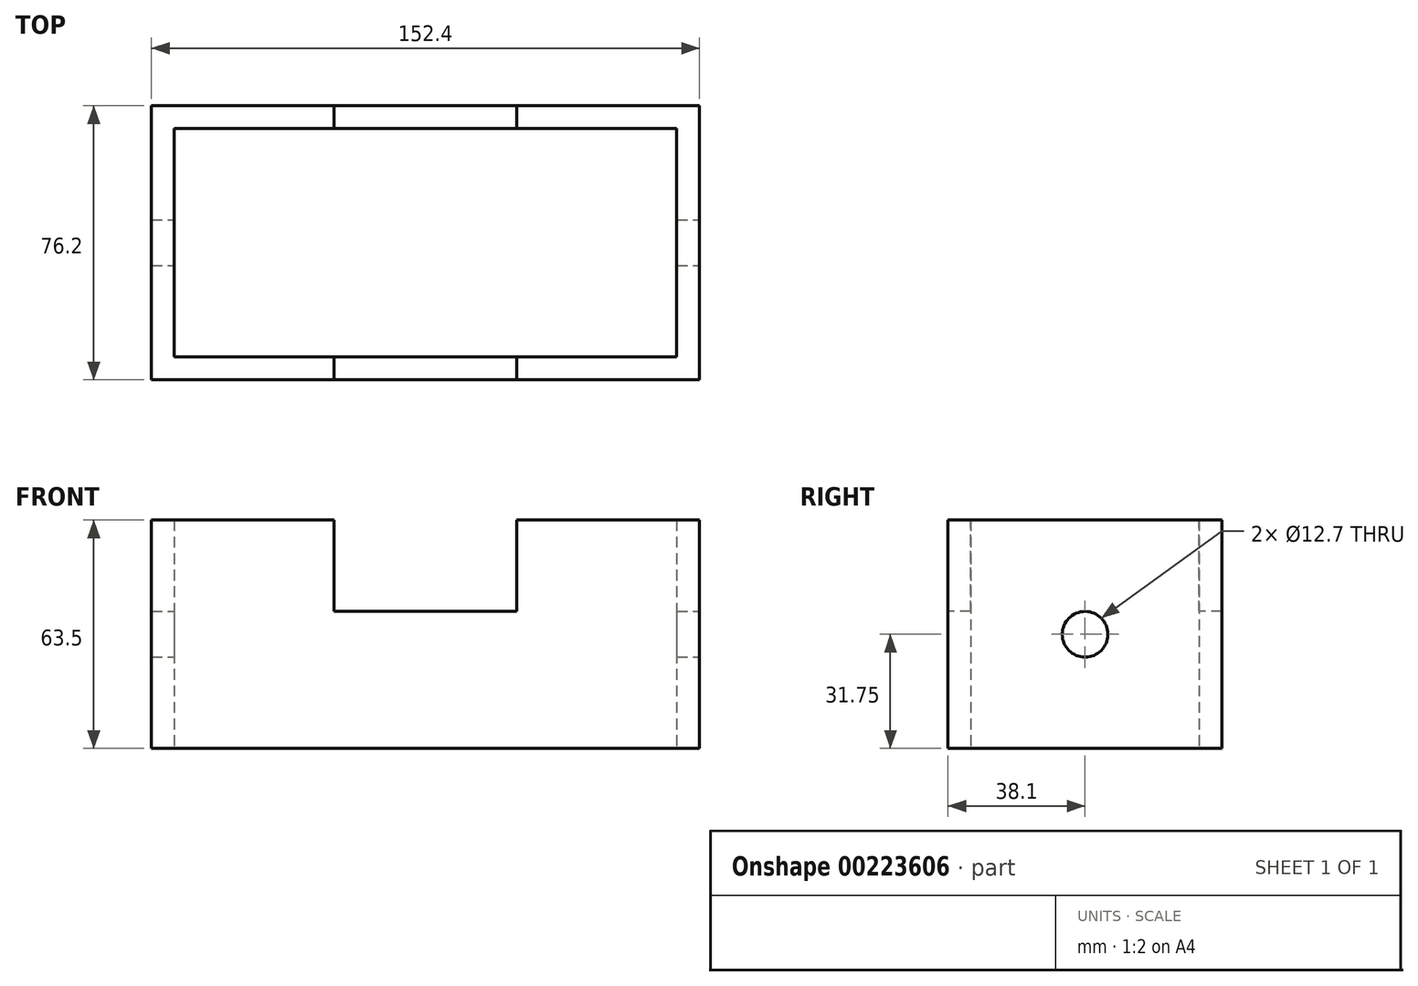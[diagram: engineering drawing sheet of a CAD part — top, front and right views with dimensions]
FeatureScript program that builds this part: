
annotation { "Feature Type Name" : "Feature", "Feature Type Description" : "" }
export const myFeature = defineFeature(function(context is Context, id is Id, definition is map)
    precondition{}
    {
        {
            var Q0;
            Q0=qCreatedBy(makeId("Top.planeOp"),FACE);
            var sketch = newSketch(context, id + "F0", { "sketchPlane" : qUnion([Q0])});
            skLineSegment(sketch, "E0.bottom", {"start": v(-76.2, -38.1) * mm, "end": v(76.2, -38.1) * mm});
            skLineSegment(sketch, "E0.top", {"start": v(-76.2, 38.1) * mm, "end": v(76.2, 38.1) * mm});
            skLineSegment(sketch, "E0.left", {"start": v(-76.2, -38.1) * mm, "end": v(-76.2, 38.1) * mm});
            skLineSegment(sketch, "E0.right", {"start": v(76.2, -38.1) * mm, "end": v(76.2, 38.1) * mm});
            skPoint(sketch, "E0.middle", {"position": v(0, 0) * mm});
            skLineSegment(sketch, "E1.bottom", {"start": v(-69.85, -31.75) * mm, "end": v(69.85, -31.75) * mm});
            skLineSegment(sketch, "E1.top", {"start": v(-69.85, 31.75) * mm, "end": v(69.85, 31.75) * mm});
            skLineSegment(sketch, "E1.left", {"start": v(-69.85, -31.75) * mm, "end": v(-69.85, 31.75) * mm});
            skLineSegment(sketch, "E1.right", {"start": v(69.85, -31.75) * mm, "end": v(69.85, 31.75) * mm});
            skSolve(sketch);
        }
        {
            var Q0;
            Q0=makeQuery(id+"F0.imprint","IMPRINT",FACE,{"disambiguationData":[TD([[makeQuery(id+"F0.imprint","IMPRINT",EDGE,{"derivedFrom":sQuery(id+"F0.wireOp",EDGE,"E0.bottom")}),1.0]])]});
            extrude(context, id + "F1", {"entities" : qUnion([Q0]), "depth" : 63.5 * mm});
        }
        {
            var Q0;
            Q0=makeQuery(id+"F1.opExtrude","SWEPT_FACE",FACE,{"disambiguationData":[OSD([sQuery(id+"F0.wireOp",EDGE,"E0.bottom")])]});
            var sketch = newSketch(context, id + "F2", { "sketchPlane" : qUnion([Q0])});
            skLineSegment(sketch, "E2.bottom", {"start": v(-25.4, 63.5) * mm, "end": v(25.4, 63.5) * mm});
            skLineSegment(sketch, "E2.top", {"start": v(-25.4, 38.1) * mm, "end": v(25.4, 38.1) * mm});
            skLineSegment(sketch, "E2.left", {"start": v(-25.4, 63.5) * mm, "end": v(-25.4, 38.1) * mm});
            skLineSegment(sketch, "E2.right", {"start": v(25.4, 63.5) * mm, "end": v(25.4, 38.1) * mm});
            skSolve(sketch);
        }
        {
            var Q0;
            Q0=makeQuery(id+"F2.imprint","IMPRINT",FACE,{"disambiguationData":[TD([[makeQuery(id+"F2.imprint","IMPRINT",EDGE,{"derivedFrom":sQuery(id+"F2.wireOp",EDGE,"E2.bottom")}),-1.0]])]});
            extrude(context, id + "F3", {"entities" : qUnion([Q0]), "operationType" : NewBodyOperationType.REMOVE, "oppositeDirection" : true, "depth" : 81.03 * mm});
        }
        {
            var Q0;
            Q0=makeQuery(id+"F1.opExtrude","SWEPT_FACE",FACE,{"disambiguationData":[OSD([sQuery(id+"F0.wireOp",EDGE,"E0.right")])]});
            var sketch = newSketch(context, id + "F4", { "sketchPlane" : qUnion([Q0])});
            skCircle(sketch, "E3", {"center": v(0, 31.75) * mm, "radius": 6.35 * mm});
            skPoint(sketch, "E3.centerSnap0", {"position": v(-38.1, 31.75) * mm});
            skPoint(sketch, "E3.centerSnap1", {"position": v(0, 63.5) * mm});
            skSolve(sketch);
        }
        {
            var Q0;
            Q0=makeQuery(id+"F4.imprint","IMPRINT",FACE,{"disambiguationData":[TD([[makeQuery(id+"F4.imprint","IMPRINT",EDGE,{"derivedFrom":sQuery(id+"F4.wireOp",EDGE,"E3")}),1.0]])]});
            extrude(context, id + "F5", {"entities" : qUnion([Q0]), "operationType" : NewBodyOperationType.REMOVE, "oppositeDirection" : true, "depth" : 156.97 * mm});
        }
    });
